# Revit family: PFX_A3-Basins-w-Vanity-Unit
name_source: partatom
category: Furniture
revit_build: Autodesk Revit 2016 (Build: 20150220_1215(x64)
units: mm (PartAtom-declared; Revit-internal decimal feet)

## family parameters
Always vertical = Yes
Cut with Voids When Loaded = No
Room Calculation Point = No
Shared = No
Work Plane-Based = No

## types (1)
- Vanity Unit
    Height = 750 mm  [stored 2.46063 ft]
    Keynote = N13/180
    Material - Cupboards = Laminate - White
    Material - Worktop = Laminate Worktop
    Material Basins = Porcelain
    Material Taps = Metal - Chrome Polished
    Plinth Height = 125 mm  [stored 0.410105 ft]
    Plinth Setback = 45 mm  [stored 0.147638 ft]
    Spacing = 550 mm
    SplashBack Height = 150 mm
    Width = 275 mm

note: [stored X ft] marks values corroborated as IEEE doubles in the binary element streams (Revit-internal decimal feet)

## geometry (parser evidence)
native form markers: Sweep x6
no freeform markers — native parametric forms only
